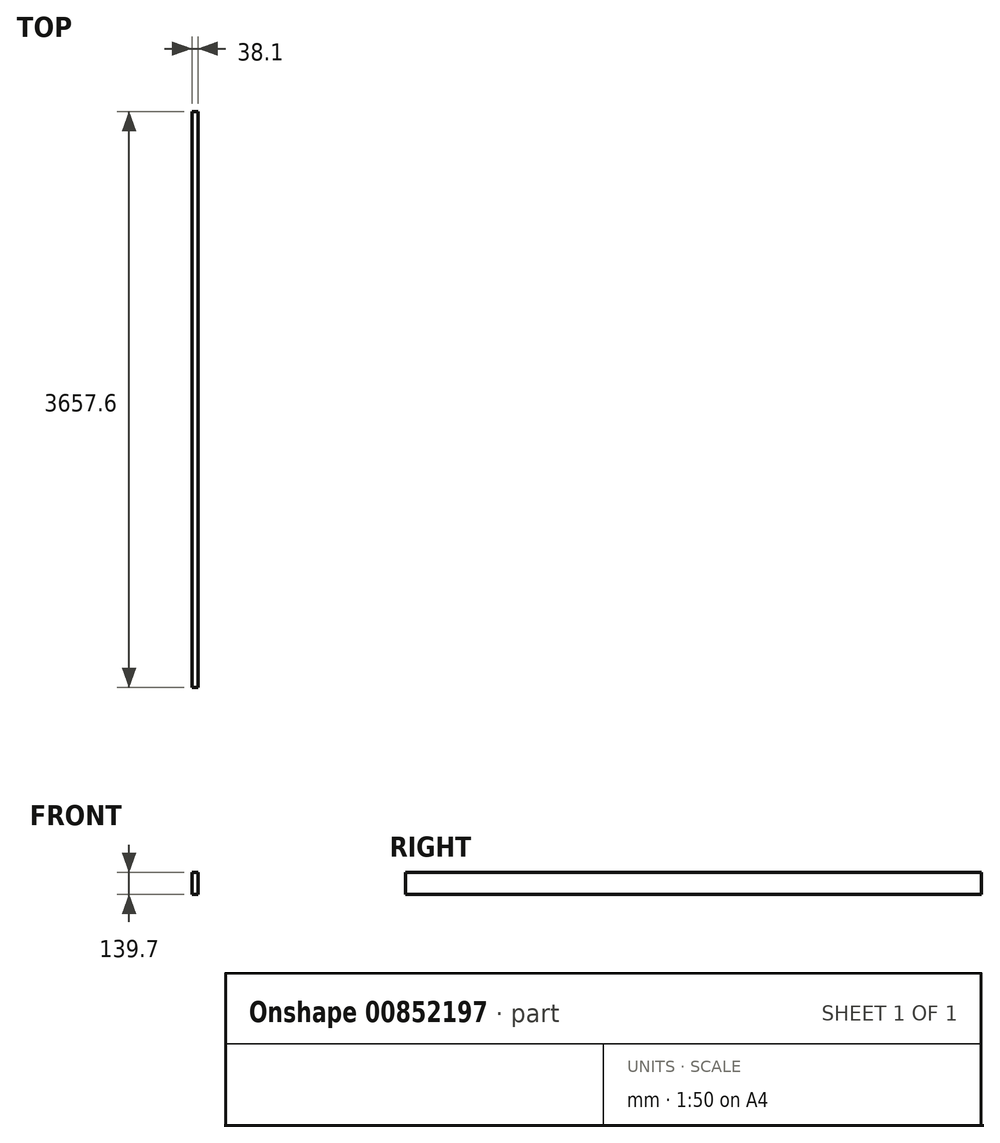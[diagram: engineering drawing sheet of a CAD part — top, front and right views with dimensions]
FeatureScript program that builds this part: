
annotation { "Feature Type Name" : "Feature", "Feature Type Description" : "" }
export const myFeature = defineFeature(function(context is Context, id is Id, definition is map)
    precondition{}
    {
        {
            var Q0;
            Q0=qCreatedBy(makeId("Front.planeOp"),FACE);
            var sketch = newSketch(context, id + "F0", { "sketchPlane" : qUnion([Q0])});
            skLineSegment(sketch, "E0.bottom", {"start": v(19.05, -69.85) * mm, "end": v(-19.05, -69.85) * mm});
            skLineSegment(sketch, "E0.top", {"start": v(19.05, 69.85) * mm, "end": v(-19.05, 69.85) * mm});
            skLineSegment(sketch, "E0.left", {"start": v(19.05, -69.85) * mm, "end": v(19.05, 69.85) * mm});
            skLineSegment(sketch, "E0.right", {"start": v(-19.05, -69.85) * mm, "end": v(-19.05, 69.85) * mm});
            skPoint(sketch, "E0.middle", {"position": v(0, 0) * mm});
            skSolve(sketch);
        }
        {
            var Q0;
            Q0=qSketchRegion(id+"F0",true);
            extrude(context, id + "F1", {"entities" : qUnion([Q0]), "depth" : 3657.6 * mm, "offsetDistance" : 25.4 * mm});
        }
    });
